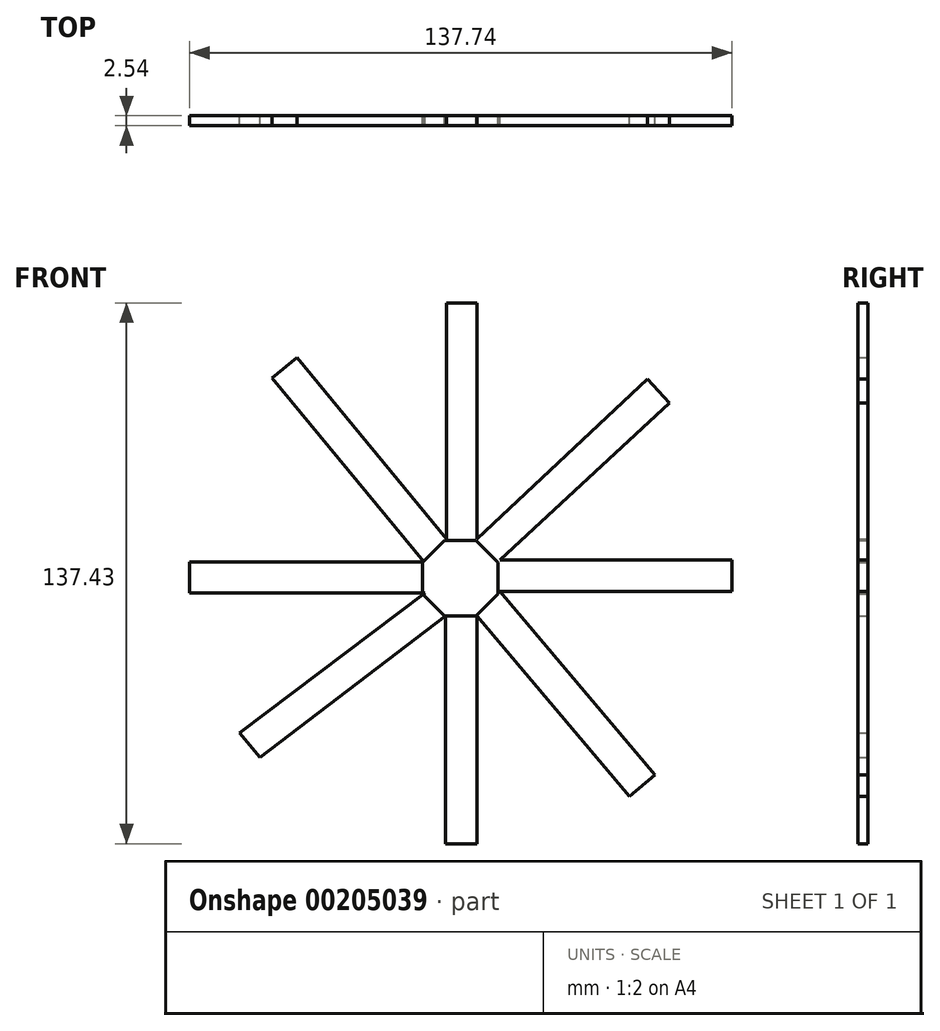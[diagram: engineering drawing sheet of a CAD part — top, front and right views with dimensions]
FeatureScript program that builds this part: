
annotation { "Feature Type Name" : "Feature", "Feature Type Description" : "" }
export const myFeature = defineFeature(function(context is Context, id is Id, definition is map)
    precondition{}
    {
        {
            var Q0;
            Q0=qCreatedBy(makeId("Front.planeOp"),FACE);
            var sketch = newSketch(context, id + "F0", { "sketchPlane" : qUnion([Q0])});
            skCircle(sketch, "E0.cCircle", {"center": v(0, 6.99) * mm, "radius": 10.4 * mm, "construction": true});
            skLineSegment(sketch, "E0.0", {"start": v(9.6, 10.97) * mm, "end": v(9.6, 3) * mm});
            skLineSegment(sketch, "E0.1", {"start": v(9.6, 3) * mm, "end": v(3.98, -2.62) * mm});
            skLineSegment(sketch, "E0.2", {"start": v(3.98, -2.62) * mm, "end": v(-3.98, -2.62) * mm});
            skLineSegment(sketch, "E0.3", {"start": v(-3.98, -2.62) * mm, "end": v(-9.6, 3) * mm});
            skLineSegment(sketch, "E0.4", {"start": v(-9.6, 3) * mm, "end": v(-9.6, 10.97) * mm});
            skLineSegment(sketch, "E0.5", {"start": v(-9.6, 10.97) * mm, "end": v(-3.98, 16.6) * mm});
            skLineSegment(sketch, "E0.6", {"start": v(-3.98, 16.6) * mm, "end": v(3.98, 16.6) * mm});
            skLineSegment(sketch, "E0.7", {"start": v(3.98, 16.6) * mm, "end": v(9.6, 10.97) * mm});
            skSolve(sketch);
        }
        {
            var Q0;
            Q0=makeQuery(id+"F0.imprint","IMPRINT",FACE,{"disambiguationData":[TD([[makeQuery(id+"F0.imprint","IMPRINT",EDGE,{"derivedFrom":sQuery(id+"F0.wireOp",EDGE,"E0.0")}),-1.0]])]});
            var sketch = newSketch(context, id + "F1", { "sketchPlane" : qUnion([Q0])});
            skLineSegment(sketch, "E1", {"start": v(4.27, 16.87) * mm, "end": v(4.27, 76.92) * mm});
            skLineSegment(sketch, "E2", {"start": v(4.58, 76.92) * mm, "end": v(-3.47, 76.92) * mm});
            skLineSegment(sketch, "E3", {"start": v(-3.47, 76.92) * mm, "end": v(-3.47, 16.87) * mm});
            skLineSegment(sketch, "E4", {"start": v(-3.47, 16.87) * mm, "end": v(-41.54, 62.99) * mm});
            skLineSegment(sketch, "E5", {"start": v(-41.54, 62.99) * mm, "end": v(-47.8, 57.82) * mm});
            skLineSegment(sketch, "E6", {"start": v(-47.8, 57.82) * mm, "end": v(-9.23, 11.09) * mm});
            skLineSegment(sketch, "E7", {"start": v(-9.23, 11.09) * mm, "end": v(-68.78, 11.09) * mm});
            skLineSegment(sketch, "E8", {"start": v(-68.78, 11.09) * mm, "end": v(-68.78, 3.25) * mm});
            skLineSegment(sketch, "E9", {"start": v(-68.78, 3.25) * mm, "end": v(-9.04, 3.25) * mm});
            skLineSegment(sketch, "E10", {"start": v(-3.78, -2.63) * mm, "end": v(-3.78, -60.5) * mm});
            skLineSegment(sketch, "E11", {"start": v(-3.78, -60.5) * mm, "end": v(4.27, -60.5) * mm});
            skLineSegment(sketch, "E12", {"start": v(4.27, -60.5) * mm, "end": v(4.27, -2.63) * mm});
            skLineSegment(sketch, "E13", {"start": v(4.27, -2.63) * mm, "end": v(42.96, -48.44) * mm});
            skLineSegment(sketch, "E14", {"start": v(42.96, -48.44) * mm, "end": v(49.4, -43) * mm});
            skLineSegment(sketch, "E15", {"start": v(49.4, -43) * mm, "end": v(10.03, 3.62) * mm});
            skLineSegment(sketch, "E16", {"start": v(10.03, 3.62) * mm, "end": v(68.96, 3.62) * mm});
            skLineSegment(sketch, "E17", {"start": v(68.96, 11.6) * mm, "end": v(68.96, 3.62) * mm});
            skLineSegment(sketch, "E18", {"start": v(68.96, 11.6) * mm, "end": v(10.03, 11.6) * mm});
            skLineSegment(sketch, "E19", {"start": v(10.03, 11.6) * mm, "end": v(53.18, 51.54) * mm});
            skLineSegment(sketch, "E20", {"start": v(53.18, 51.54) * mm, "end": v(47.54, 57.62) * mm});
            skLineSegment(sketch, "E21", {"start": v(47.54, 57.62) * mm, "end": v(4.27, 16.87) * mm});
            skLineSegment(sketch, "E22", {"start": v(-9.04, 3.25) * mm, "end": v(-56.1, -32.34) * mm});
            skLineSegment(sketch, "E23", {"start": v(-56.1, -32.34) * mm, "end": v(-50.85, -38.55) * mm});
            skLineSegment(sketch, "E24", {"start": v(-50.85, -38.55) * mm, "end": v(-3.78, -2.63) * mm});
            skSolve(sketch);
        }
        {
            var Q0;
            Q0=qSketchRegion(id+"F0",true);
            var Q1;
            Q1=qSketchRegion(id+"F1",true);
            extrude(context, id + "F2", {"entities" : qUnion([Q0, Q1]), "depth" : 2.54 * mm});
        }
    });
